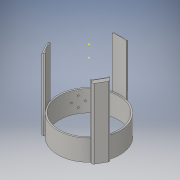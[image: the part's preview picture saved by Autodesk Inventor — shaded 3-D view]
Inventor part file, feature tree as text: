
AUTODESK INVENTOR PART (.ipt)
format: ipt  version: 2016 (Build 200138000, 138)  size: 264,192 bytes
history: native  units: in
note: dims shown in document units (in); Inventor stores cm internally (conversion verified against a paired STEP export)
features: sketch x17, extrude x14, plane x3, chamfer x2, fillet x1, revolve x1
ambient origin geometry x8: Origin, YZ Plane, XZ Plane, XY Plane, X Axis, Y Axis, Z Axis, Center Point
bodies: Solid1 (feature_tree)
feature tree (38):
  extrude  "Extrusion1"  Depth=0.3in TaperAngle=0.0deg
  extrude  "Extrusion2"  Depth=0.125in TaperAngle=0.0deg
  extrude  "Extrusion3"  Depth=3.875in
  sketch  "Sketch4"  dims[d9=0.125in d10=0.0in d11=4.0in]
  extrude  "Extrusion4"  Depth=4.0in
  extrude  "Extrusion5"  Depth=4.5in
  extrude  "Extrusion6"  Depth=0.1in TaperAngle=45.0deg
  chamfer  "Chamfer1"  Distance=2.3622in Angle=360.0deg
  extrude  "Extrusion7"  Depth=1.0in
  extrude  "Extrusion8"  Depth=5.0in TaperAngle=0.0deg
  extrude  "Extrusion9"  Depth=0.375in TaperAngle=0.0deg
  extrude  "Extrusion10"  Depth=0.375in TaperAngle=0.0deg
  extrude  "Extrusion11"  Depth=0.5in
  sketch  "Sketch13"  dims[d39=20.0in d40=0.0in d41=0.5in]
  extrude  "Extrusion12"  Depth=0.15in
  chamfer  "Chamfer2"  Distance=1.1811in Angle=360.0deg
  fillet  "Fillet1"  Radius=0.125in
  plane  "Work Plane1"
  revolve  "Revolution1"  [1 undecoded]
  plane  "Work Plane3"
  extrude  "Extrusion13"  TaperAngle=90.0deg  [1 undecoded]
  extrude  "Extrusion15"  [1 undecoded]
  sketch  "Sketch1"  dims[d0=4.0in d1=0.3in d2=0.0in]
  sketch  "Sketch2"  dims[d3=3.875in d4=0.125in d5=0.0in]
  sketch  "Sketch3"  dims[d6=0.3in d7=0.0in d8=3.875in]
  sketch  "Sketch5"  dims[d12=0.2in d13=0.0in d14=4.5in]
  sketch  "Sketch6"  dims[d15=0.24in d16=0.0in d17=0.1in d18=0.125in d19=45.0deg]
  sketch  "Sketch7"  dims[d20=0.138in]
  sketch  "Sketch8"  dims[d21=2.125in d22=2.3622in d24=360.0deg]
  sketch  "Sketch9"  dims[d26=0.24in d27=0.0in d28=1.0in]
  sketch  "Sketch10"  dims[d29=0.1in d31=5.0in d32=0.0in]
  sketch  "Sketch11"  dims[d33=3.0in d34=0.375in d35=0.0in]
  sketch  "Sketch12"  dims[d36=1.0in d37=0.375in d38=0.0in]
  sketch  "Sketch14"  dims[d42=0.5in d43=0.15in d44=1.1811in d46=360.0deg]
  sketch  "Sketch15"  dims[d48=5.0in d49=0.2in d50=0.0in d51=0.0in]
  plane  "Work Plane2"
  sketch  "Sketch16"  dims[d52=0.125in d53=0.125in d54=45.0deg d55=0.125in]
  sketch  "Sketch18"  dims[d58=0.1in d59=1.527in d60=90.0deg d61=-4.125in d64=0.118in d65=0.118in d66=0.118in d67=0.118in d68=0.74in d69=0.74in d70=0.74in d71=0.74in d72=5.0in d73=0.0in d78=1.04in d79=0.0in]
note: 3 required parameter values undecoded (feature->parameter linkage not recoverable at this tier; creation-order binding heuristic only, values carry confidence <= 0.55)